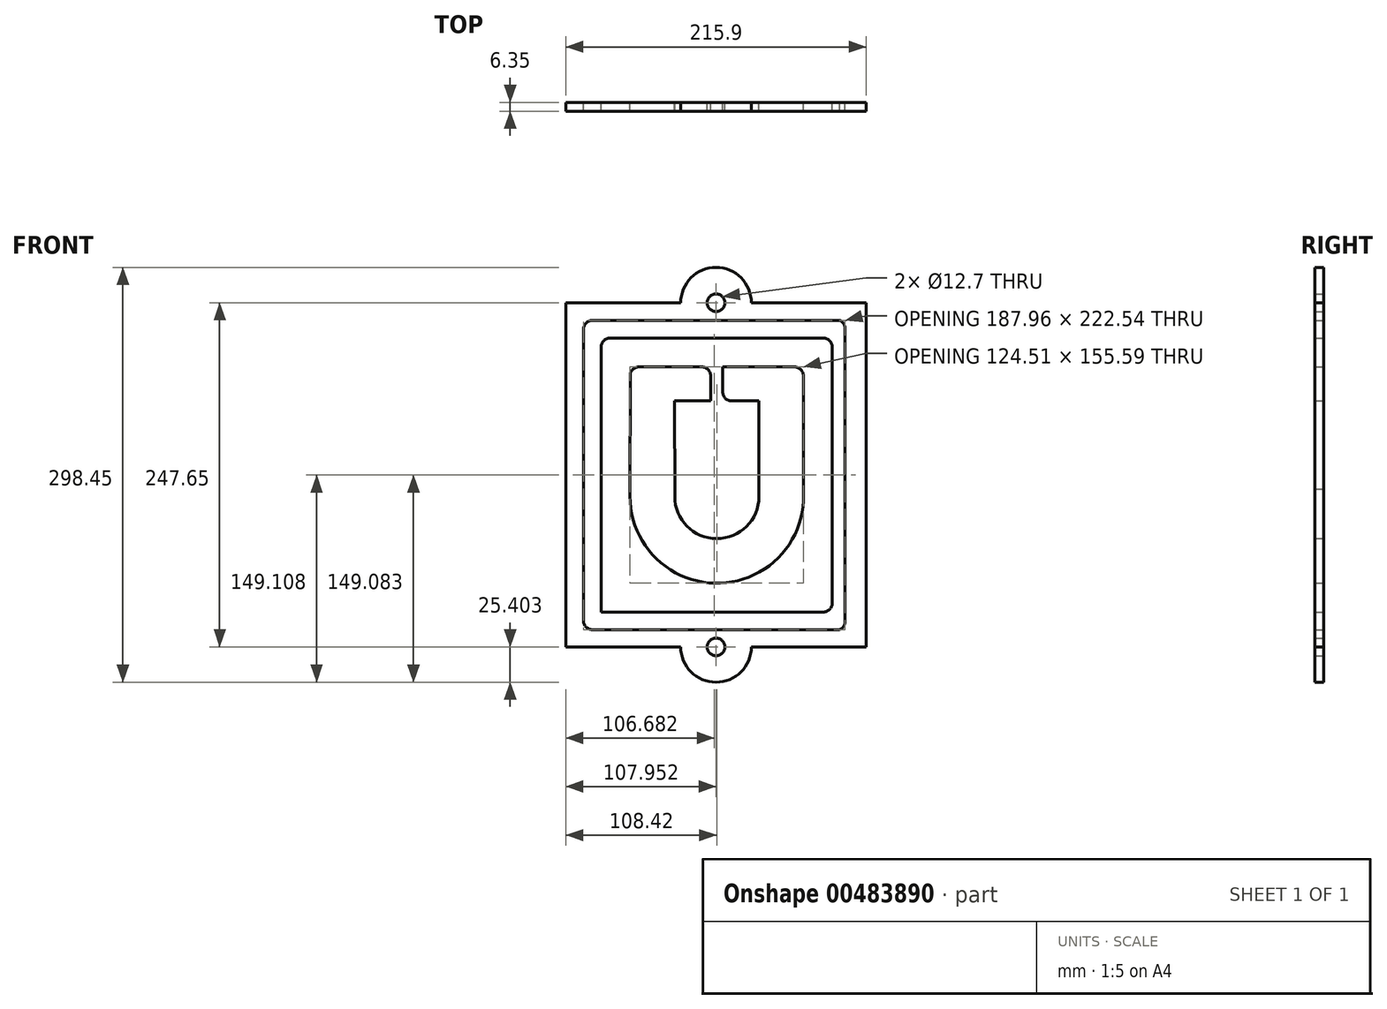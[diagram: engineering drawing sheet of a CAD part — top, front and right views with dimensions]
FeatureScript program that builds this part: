
annotation { "Feature Type Name" : "Feature", "Feature Type Description" : "" }
export const myFeature = defineFeature(function(context is Context, id is Id, definition is map)
    precondition{}
    {
        {
            var Q0;
            Q0=qCreatedBy(makeId("Front.planeOp"),FACE);
            var sketch = newSketch(context, id + "F0", { "sketchPlane" : qUnion([Q0])});
            skLineSegment(sketch, "E0.bottom", {"start": v(96.66, 108.78) * mm, "end": v(45.08, 108.78) * mm});
            skLineSegment(sketch, "E0.top", {"start": v(71.14, 84.27) * mm, "end": v(51.43, 84.27) * mm});
            skLineSegment(sketch, "E1.left", {"start": v(36.4, 102.43) * mm, "end": v(36.4, 84.27) * mm});
            skLineSegment(sketch, "E1.right", {"start": v(45.08, 108.78) * mm, "end": v(45.08, 90.62) * mm});
            skLineSegment(sketch, "E2.trimOffspring", {"start": v(30.05, 108.78) * mm, "end": v(-15.15, 108.78) * mm});
            skLineSegment(sketch, "E3.trimOffspring", {"start": v(36.4, 84.27) * mm, "end": v(10.5, 84.27) * mm});
            skLineSegment(sketch, "E4", {"start": v(71.14, 84.27) * mm, "end": v(71.14, 15.4) * mm});
            skLineSegment(sketch, "E5", {"start": v(10.5, 84.27) * mm, "end": v(10.59, 15.63) * mm});
            skArc(sketch, "E6", {"start": v(10.59, 15.63) * mm, "mid": v(40.75, -14.76) * mm, "end": v(71.14, 15.4) * mm});
            skArc(sketch, "E7", {"start": v(-21.5, 15.7) * mm, "mid": v(43.43, -46.8) * mm, "end": v(103, 20.83) * mm});
            skLineSegment(sketch, "E8.bottom", {"start": v(117.4, 129.53) * mm, "end": v(-35.92, 129.53) * mm});
            skLineSegment(sketch, "E8.top", {"start": v(117.4, -67.6) * mm, "end": v(-42.27, -67.6) * mm});
            skLineSegment(sketch, "E8.left", {"start": v(123.74, 123.18) * mm, "end": v(123.74, -61.26) * mm});
            skLineSegment(sketch, "E8.right", {"start": v(-42.27, 123.18) * mm, "end": v(-42.27, -67.6) * mm});
            skLineSegment(sketch, "E9.left", {"start": v(-54.97, 135.88) * mm, "end": v(-54.97, -73.96) * mm});
            skLineSegment(sketch, "E9.right", {"start": v(133, 136.41) * mm, "end": v(133, -74.49) * mm});
            skLineSegment(sketch, "E10", {"start": v(103, 20.83) * mm, "end": v(103, 102.43) * mm});
            skLineSegment(sketch, "E11", {"start": v(-21.5, 102.43) * mm, "end": v(-21.5, 15.7) * mm});
            skPoint(sketch, "E12.visualSharp", {"position": v(36.4, 108.78) * mm});
            skArc(sketch, "E12.filletArc", {"start": v(36.4, 102.43) * mm, "mid": v(34.54, 106.92) * mm, "end": v(30.05, 108.78) * mm});
            skPoint(sketch, "E13.visualSharp", {"position": v(45.08, 84.27) * mm});
            skArc(sketch, "E13.filletArc", {"start": v(45.08, 90.62) * mm, "mid": v(46.94, 86.13) * mm, "end": v(51.43, 84.27) * mm});
            skPoint(sketch, "E14.visualSharp", {"position": v(103, 108.78) * mm});
            skArc(sketch, "E14.filletArc", {"start": v(103, 102.43) * mm, "mid": v(101.15, 106.92) * mm, "end": v(96.66, 108.78) * mm});
            skPoint(sketch, "E15.visualSharp", {"position": v(-21.5, 108.78) * mm});
            skArc(sketch, "E15.filletArc", {"start": v(-15.15, 108.78) * mm, "mid": v(-19.64, 106.92) * mm, "end": v(-21.5, 102.43) * mm});
            skArc(sketch, "E16.filletArc", {"start": v(-48.62, 142.23) * mm, "mid": v(-53.1, 140.37) * mm, "end": v(-54.97, 135.88) * mm});
            skPoint(sketch, "E17.visualSharp", {"position": v(-42.27, 129.53) * mm});
            skArc(sketch, "E17.filletArc", {"start": v(-35.92, 129.53) * mm, "mid": v(-40.4, 127.67) * mm, "end": v(-42.27, 123.18) * mm});
            skArc(sketch, "E18.filletArc", {"start": v(133, 136.41) * mm, "mid": v(131.95, 139.9) * mm, "end": v(129.18, 142.23) * mm});
            skPoint(sketch, "E19.visualSharp", {"position": v(123.74, 129.53) * mm});
            skArc(sketch, "E19.filletArc", {"start": v(123.74, 123.18) * mm, "mid": v(121.88, 127.67) * mm, "end": v(117.4, 129.53) * mm});
            skPoint(sketch, "E20.visualSharp", {"position": v(123.74, -67.6) * mm});
            skArc(sketch, "E20.filletArc", {"start": v(117.4, -67.6) * mm, "mid": v(121.88, -65.75) * mm, "end": v(123.74, -61.26) * mm});
            skPoint(sketch, "E21.visualSharp", {"position": v(133, -80.3) * mm});
            skArc(sketch, "E21.filletArc", {"start": v(129.18, -80.3) * mm, "mid": v(131.95, -77.97) * mm, "end": v(133, -74.49) * mm});
            skArc(sketch, "E22.filletArc", {"start": v(-54.97, -73.96) * mm, "mid": v(-53.1, -78.45) * mm, "end": v(-48.62, -80.3) * mm});
            skLineSegment(sketch, "E23", {"start": v(-48.62, -80.3) * mm, "end": v(129.18, -80.3) * mm});
            skLineSegment(sketch, "E24", {"start": v(-67.67, 129.53) * mm, "end": v(-67.67, 154.93) * mm});
            skLineSegment(sketch, "E25.bottom", {"start": v(-67.67, 154.93) * mm, "end": v(14.88, 154.93) * mm});
            skLineSegment(sketch, "E25.top", {"start": v(-67.67, -92.72) * mm, "end": v(14.88, -92.72) * mm});
            skLineSegment(sketch, "E25.left", {"start": v(-67.67, 154.93) * mm, "end": v(-67.67, -92.72) * mm});
            skLineSegment(sketch, "E25.right", {"start": v(148.23, 154.93) * mm, "end": v(148.23, -92.72) * mm});
            skLineSegment(sketch, "E26", {"start": v(-48.62, 142.23) * mm, "end": v(129.18, 142.23) * mm});
            skArc(sketch, "E27", {"start": v(65.68, 154.93) * mm, "mid": v(40.28, 180.33) * mm, "end": v(14.88, 154.93) * mm});
            skCircle(sketch, "E28", {"center": v(40.28, 154.93) * mm, "radius": 6.35 * mm});
            skLineSegment(sketch, "E29.trimOffspring", {"start": v(65.68, 154.93) * mm, "end": v(148.23, 154.93) * mm});
            skCircle(sketch, "E30", {"center": v(40.28, -92.72) * mm, "radius": 6.35 * mm});
            skArc(sketch, "E31.trimOffspring", {"start": v(14.88, -92.72) * mm, "mid": v(40.28, -118.12) * mm, "end": v(65.68, -92.72) * mm});
            skLineSegment(sketch, "E32.trimOffspring", {"start": v(65.68, -92.72) * mm, "end": v(148.23, -92.72) * mm});
            skSolve(sketch);
        }
        {
            var Q0;
            Q0=makeQuery(id+"F0.imprint","IMPRINT",FACE,{"disambiguationData":[TD([[makeQuery(id+"F0.imprint","IMPRINT",EDGE,{"derivedFrom":sQuery(id+"F0.wireOp",EDGE,"E0.bottom")}),-1.0]])]});
            extrude(context, id + "F1", {"entities" : qUnion([Q0]), "depth" : 6.35 * mm, "offsetDistance" : 25.4 * mm});
        }
        {
            var Q0;
            Q0=makeQuery(id+"F0.imprint","IMPRINT",FACE,{"disambiguationData":[TD([[makeQuery(id+"F0.imprint","IMPRINT",EDGE,{"derivedFrom":sQuery(id+"F0.wireOp",EDGE,"E9.left")}),-1.0]])]});
            extrude(context, id + "F2", {"entities" : qUnion([Q0]), "depth" : 6.35 * mm, "offsetDistance" : 25.4 * mm});
        }
    });
